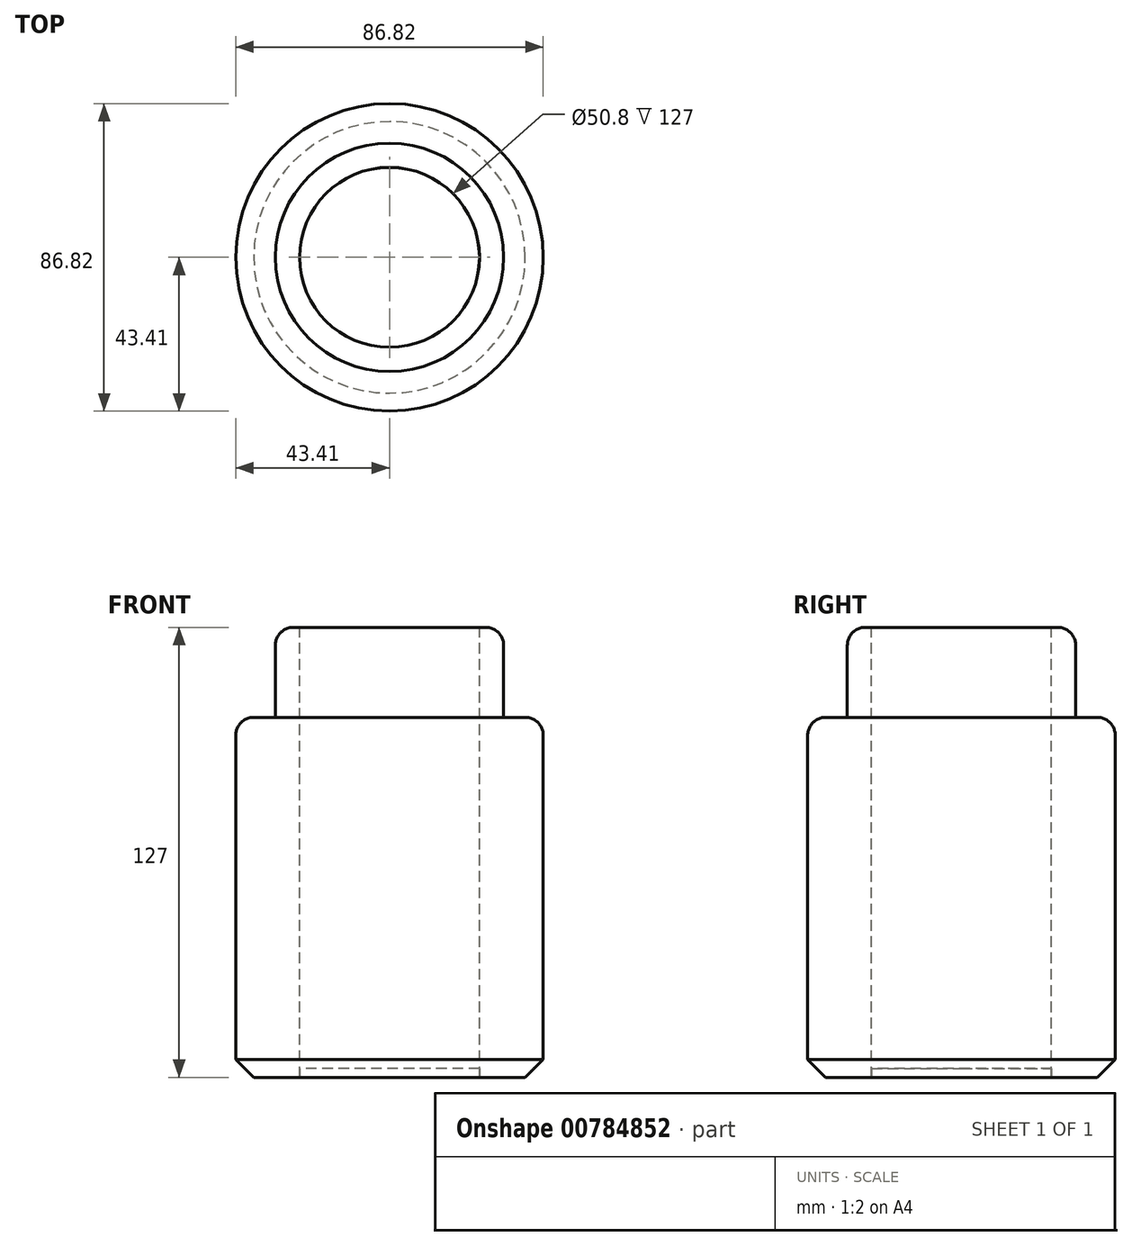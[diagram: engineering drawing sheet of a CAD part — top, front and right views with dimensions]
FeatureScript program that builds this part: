
annotation { "Feature Type Name" : "Feature", "Feature Type Description" : "" }
export const myFeature = defineFeature(function(context is Context, id is Id, definition is map)
    precondition{}
    {
        {
            var Q0;
            Q0=qCreatedBy(makeId("Top.planeOp"),FACE);
            var sketch = newSketch(context, id + "F0", { "sketchPlane" : qUnion([Q0])});
            skCircle(sketch, "E0", {"center": v(0, 0) * mm, "radius": 43.4 * mm});
            skCircle(sketch, "E1", {"center": v(0, 0) * mm, "radius": 31.87 * mm});
            skCircle(sketch, "E2", {"center": v(0, 0) * mm, "radius": 14.98 * mm});
            skSolve(sketch);
        }
        {
            var Q0;
            Q0=makeQuery(id+"F0.imprint","IMPRINT",FACE,{"disambiguationData":[TD([[makeQuery(id+"F0.imprint","IMPRINT",EDGE,{"derivedFrom":sQuery(id+"F0.wireOp",EDGE,"E0")}),1.0]])]});
            extrude(context, id + "F1", {"entities" : qUnion([Q0]), "depth" : 101.6 * mm, "offsetDistance" : 25.4 * mm});
        }
        {
            var Q0;
            Q0=qCreatedBy(makeId("Top.planeOp"),FACE);
            var sketch = newSketch(context, id + "F2", { "sketchPlane" : qUnion([Q0])});
            skCircle(sketch, "E3", {"center": v(0, 0) * mm, "radius": 32.23 * mm});
            skSolve(sketch);
        }
        {
            var Q0;
            Q0 = qSketchRegion(id + "F2", true);
            extrude(context, id + "F3", {"entities" : qUnion([Q0]), "operationType" : NewBodyOperationType.ADD, "depth" : 127 * mm, "offsetDistance" : 25.4 * mm});
        }
        {
            var Q0;
            Q0=qCreatedBy(makeId("Top.planeOp"),FACE);
            var sketch = newSketch(context, id + "F4", { "sketchPlane" : qUnion([Q0])});
            skCircle(sketch, "E4", {"center": v(0, 0) * mm, "radius": 21 * mm});
            skSolve(sketch);
        }
        {
            var Q0;
            Q0 = qSketchRegion(id + "F4", true);
            extrude(context, id + "F5", {"entities" : qUnion([Q0]), "operationType" : NewBodyOperationType.ADD, "depth" : 132.08 * mm, "offsetDistance" : 25.4 * mm});
        }
        {
            var Q0;
            Q0=makeQuery(id+"F1.opExtrude","CAP_EDGE",EDGE,{"disambiguationData":[OSD([sQuery(id+"F0.wireOp",EDGE,"E0")])],"isStart":false});
            var Q1;
            Q1=makeQuery(id+"F3.opExtrude","CAP_EDGE",EDGE,{"disambiguationData":[OSD([sQuery(id+"F2.wireOp",EDGE,"E3")])],"isStart":false});
            var Q2;
            Q2=makeQuery(id+"F5.opExtrude","CAP_EDGE",EDGE,{"disambiguationData":[OSD([sQuery(id+"F4.wireOp",EDGE,"E4")])],"isStart":false});
            fillet(context, id + "F6", {"entities" : qUnion([Q0, Q1, Q2]), "radius" : 5.08 * mm, "tangentPropagation" : true, "allowEdgeOverflow" : false});
        }
        {
            var Q0;
            Q0=makeQuery(id+"F1.opExtrude","CAP_EDGE",EDGE,{"disambiguationData":[OSD([sQuery(id+"F0.wireOp",EDGE,"E0")])],"isStart":true});
            chamfer(context, id + "F7", {"entities" : qUnion([Q0]), "width" : 5.08 * mm, "tangentPropagation" : true});
        }
        {
            var Q0;
            Q0=makeQuery(id+"F5.opExtrude","CAP_FACE",FACE,{"disambiguationData":[OSD([sQuery(id+"F4.wireOp",EDGE,"E4")])],"isStart":false});
            var sketch = newSketch(context, id + "F8", { "sketchPlane" : qUnion([Q0])});
            skCircle(sketch, "E5", {"center": v(0, 0) * mm, "radius": 15.7 * mm});
            skSolve(sketch);
        }
        {
            var Q0;
            Q0=sQuery(id+"F8.wireOp",VERTEX,"E5.center");
            var Q1;
            Q1=makeQuery(id+"F1.opExtrude","SWEPT_BODY",BODY,{"disambiguationData":[OSD([sQuery(id+"F0.wireOp",EDGE,"E0"),sQuery(id+"F0.wireOp",EDGE,"E1")])]});
            hole(context, id + "F9", {"style" : HoleStyle.SIMPLE, "endStyle" : HoleEndStyle.THROUGH, "holeDiameter" : 50.8 * mm, "majorDiameter" : 6.35 * mm, "isTappedThrough" : true, "tappedDepth" : 12.7 * mm, "tapClearance" : 3, "locations" : qUnion([Q0]), "scope" : qUnion([Q1])});
        }
        {
            var Q0;
            Q0=qCreatedBy(makeId("Top.planeOp"),FACE);
            var sketch = newSketch(context, id + "F10", { "sketchPlane" : qUnion([Q0])});
            skCircle(sketch, "E6", {"center": v(0, 0) * mm, "radius": 25.4 * mm});
            skSolve(sketch);
        }
        {
            var Q0;
            Q0 = qSketchRegion(id + "F10", true);
            extrude(context, id + "F11", {"entities" : qUnion([Q0]), "depth" : 2.54 * mm, "offsetDistance" : 25.4 * mm});
        }
    });
